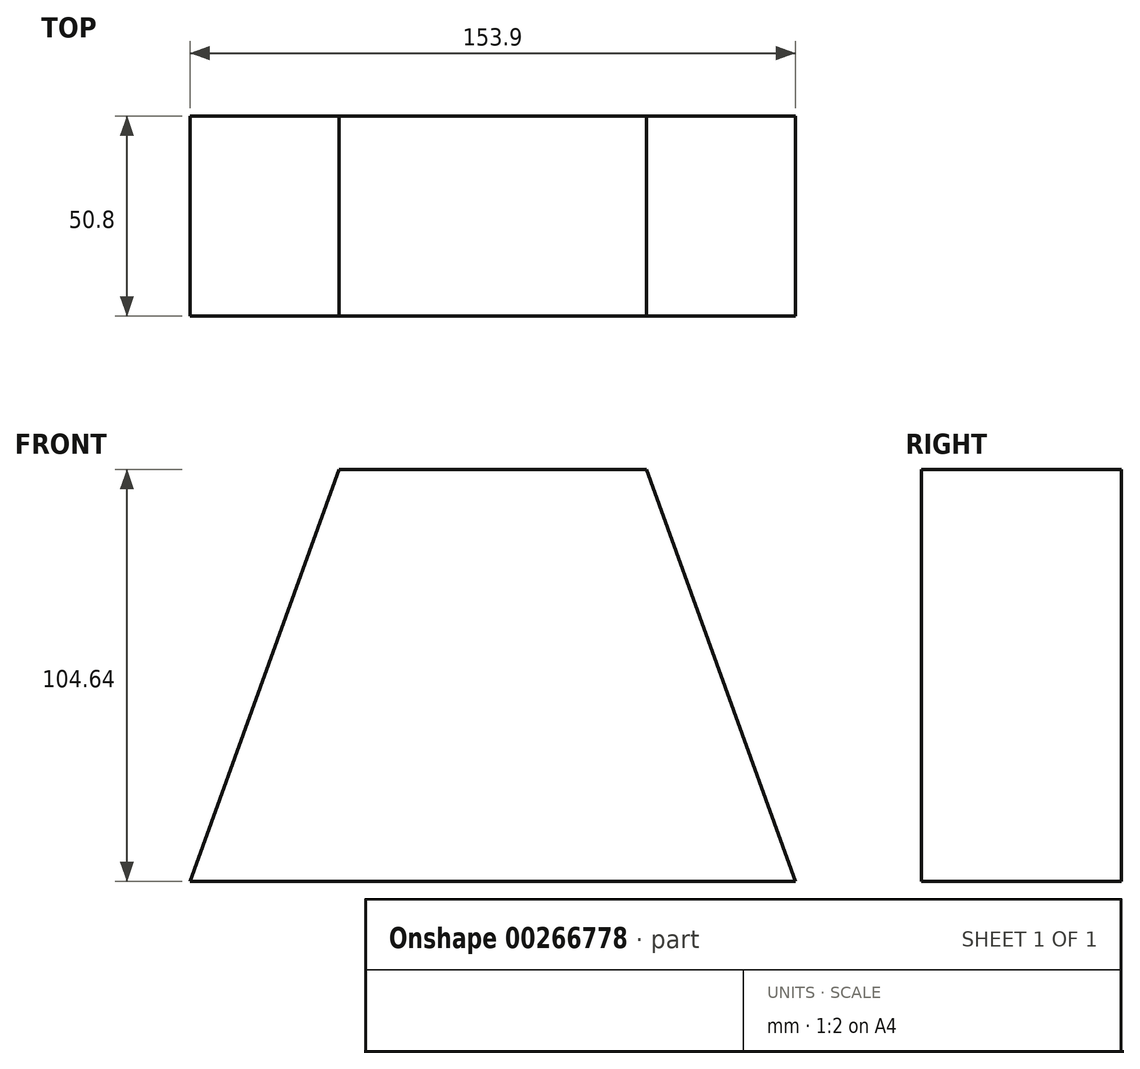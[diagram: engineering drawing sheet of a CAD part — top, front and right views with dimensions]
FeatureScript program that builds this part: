
annotation { "Feature Type Name" : "Feature", "Feature Type Description" : "" }
export const myFeature = defineFeature(function(context is Context, id is Id, definition is map)
    precondition{}
    {
        {
            var Q0;
            Q0=qCreatedBy(makeId("Front.planeOp"),FACE);
            var sketch = newSketch(context, id + "F0", { "sketchPlane" : qUnion([Q0])});
            skLineSegment(sketch, "E0", {"start": v(0, -76.51) * mm, "end": v(-76.95, -76.51) * mm});
            skLineSegment(sketch, "E1", {"start": v(-76.95, -76.51) * mm, "end": v(-39.06, 28.13) * mm});
            skLineSegment(sketch, "E2", {"start": v(0, 28.13) * mm, "end": v(-39.06, 28.13) * mm});
            skLineSegment(sketch, "E3.MirrorCS", {"start": v(0, 28.13) * mm, "end": v(39.06, 28.13) * mm});
            skLineSegment(sketch, "E4.MirrorCS", {"start": v(0, -76.51) * mm, "end": v(76.95, -76.51) * mm});
            skLineSegment(sketch, "E5.MirrorCS", {"start": v(76.95, -76.51) * mm, "end": v(39.06, 28.13) * mm});
            skSolve(sketch);
        }
        {
            var Q0;
            Q0 = qSketchRegion(id + "F0", true);
            extrude(context, id + "F1", {"entities" : qUnion([Q0]), "depth" : 50.8 * mm});
        }
    });
